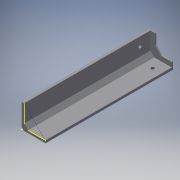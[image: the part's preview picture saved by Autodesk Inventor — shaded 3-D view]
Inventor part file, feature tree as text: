
AUTODESK INVENTOR PART (.ipt)
format: ipt  version: 2018 (Build 220112000, 112)  size: 190,464 bytes
history: native  units: in
note: dims shown in document units (in); Inventor stores cm internally (conversion verified against a paired STEP export)
features: sketch x8, extrude x3, hole x3, plane x1, fillet x1
ambient origin geometry x8: Origin, YZ Plane, XZ Plane, XY Plane, X Axis, Y Axis, Z Axis, Center Point
bodies: Solid1 (feature_tree)
feature tree (16):
  extrude  "Extrusion1"  Depth=0.75in
  extrude  "Extrusion2"  Depth=0.08in
  plane  "Work Plane1"
  extrude  "Extrusion4"  Depth=4.0in TaperAngle=0.0deg
  sketch  "Sketch6"  dims[d11=0.23in d15=0.23in d16=180.0deg]
  hole  "Hole1"  [1 undecoded]
  fillet  "Fillet1"  [1 undecoded]
  hole  "Hole2"  [1 undecoded]
  hole  "Hole3"  [1 undecoded]
  sketch  "Sketch10"  dims[d37=0.05in d38=0.6in d39=180.0deg d40=0.25in d41=0.4in d42=0.25in d43=0.5in d44=0.2in d45=0.0in d46=0.25in d47=0.25in d48=0.75in d49=0.375in d50=0.25in d51=0.5635in d52=1.0in d53=0.8108in d54=0.05in d55=0.28in d56=0.36in d57=0.1in d58=0.75in d59=0.375in d60=0.25in d61=0.5635in d62=1.0in d63=0.8108in d64=0.28in d65=0.36in d66=0.1in d67=0.75in d68=0.375in d69=0.25in d70=0.5635in d71=1.0in d72=0.8108in d73=0.1in d74=0.6793in d75=0.4in]
  sketch  "Sketch1"  dims[d0=0.75in d1=0.75in]
  sketch  "Sketch2"  dims[d2=0.08in d3=0.08in]
  sketch  "Sketch5"  dims[d8=0.15in d9=4.0in d10=0.0in]
  sketch  "Sketch7"  dims[d18=90.0deg d20=45.0deg]
  sketch  "Sketch8"  dims[d21=0.4in d22=0.04in d23=0.0in]
  sketch  "Sketch9"  dims[d30=0.5in]
note: 4 required parameter values undecoded (feature->parameter linkage not recoverable at this tier; creation-order binding heuristic only, values carry confidence <= 0.55)
